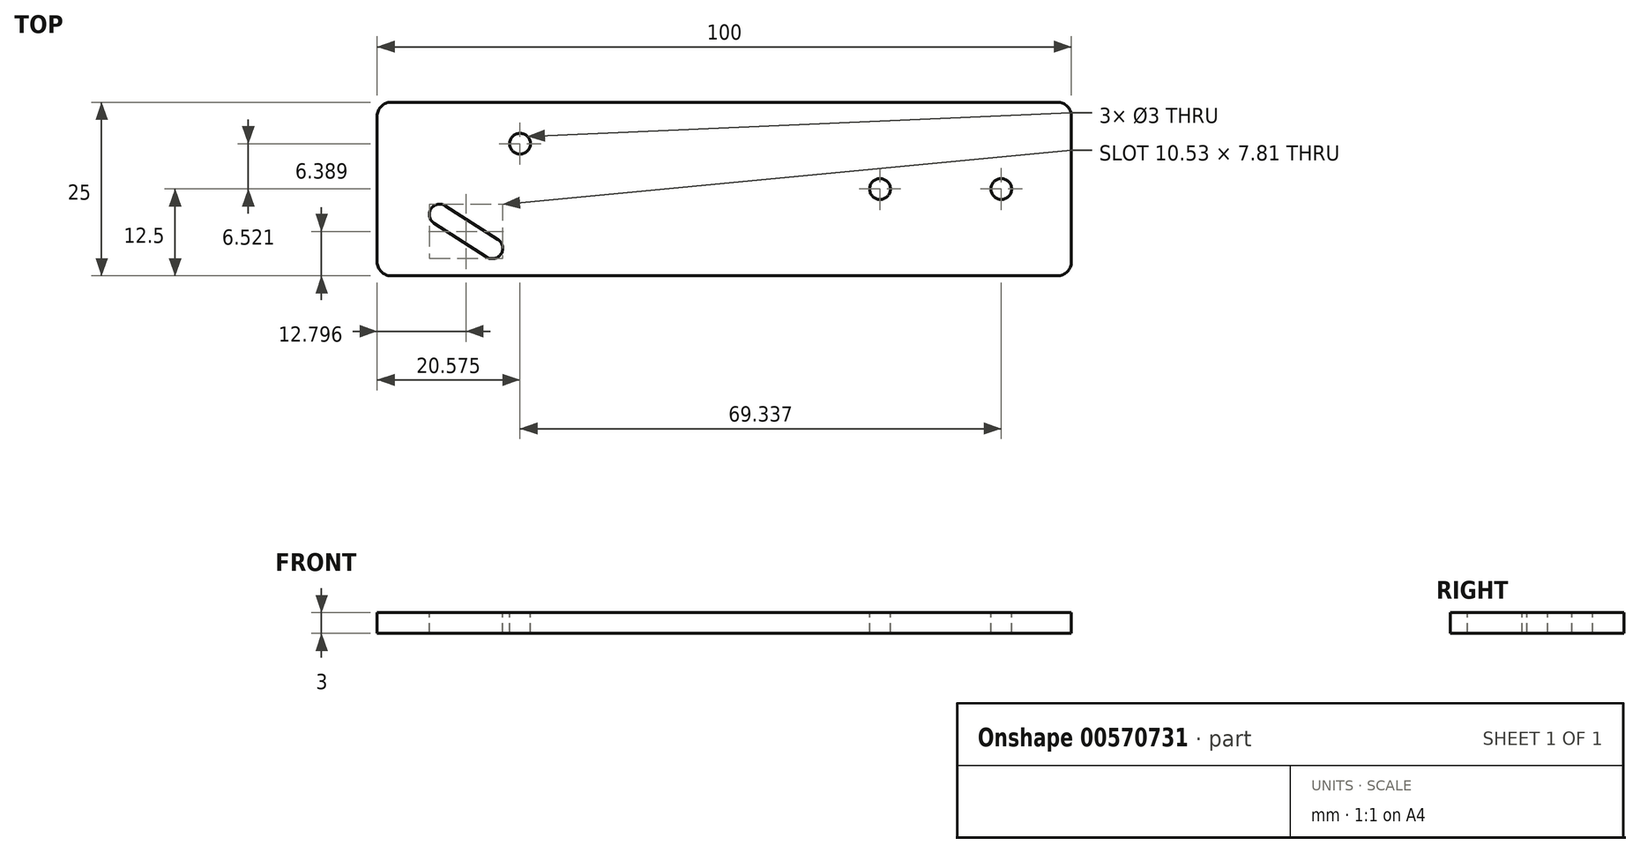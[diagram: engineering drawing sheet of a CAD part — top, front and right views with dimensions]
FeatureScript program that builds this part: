
annotation { "Feature Type Name" : "Feature", "Feature Type Description" : "" }
export const myFeature = defineFeature(function(context is Context, id is Id, definition is map)
    precondition{}
    {
        {
            var Q0;
            Q0=qCreatedBy(makeId("Top.planeOp"),FACE);
            var sketch = newSketch(context, id + "F0", { "sketchPlane" : qUnion([Q0])});
            skLineSegment(sketch, "E0.bottom", {"start": v(48, 12.5) * mm, "end": v(-48, 12.5) * mm});
            skLineSegment(sketch, "E0.top", {"start": v(48, -12.5) * mm, "end": v(-48, -12.5) * mm});
            skLineSegment(sketch, "E0.left", {"start": v(50, 10.5) * mm, "end": v(50, -10.5) * mm});
            skLineSegment(sketch, "E0.right", {"start": v(-50, 10.5) * mm, "end": v(-50, -10.5) * mm});
            skPoint(sketch, "E0.middle", {"position": v(0, 0) * mm});
            skCircle(sketch, "E1", {"center": v(-29.43, 6.52) * mm, "radius": 1.5 * mm});
            skLineSegment(sketch, "E2", {"start": v(-41.8, -4.95) * mm, "end": v(-34.22, -9.8) * mm});
            skLineSegment(sketch, "E3", {"start": v(-32.15, -9.35) * mm, "end": v(-32.15, -9.35) * mm});
            skLineSegment(sketch, "E4", {"start": v(-32.6, -7.28) * mm, "end": v(-40.18, -2.42) * mm});
            skLineSegment(sketch, "E5", {"start": v(-42.26, -2.87) * mm, "end": v(-42.26, -2.87) * mm});
            skPoint(sketch, "E6.visualSharp", {"position": v(-41.45, -1.61) * mm});
            skArc(sketch, "E6.filletArc", {"start": v(-40.18, -2.42) * mm, "mid": v(-41.31, -2.22) * mm, "end": v(-42.26, -2.87) * mm});
            skPoint(sketch, "E7.visualSharp", {"position": v(-43.06, -4.14) * mm});
            skArc(sketch, "E7.filletArc", {"start": v(-42.26, -2.87) * mm, "mid": v(-42.46, -4) * mm, "end": v(-41.8, -4.95) * mm});
            skPoint(sketch, "E8.visualSharp", {"position": v(-32.96, -10.61) * mm});
            skArc(sketch, "E8.filletArc", {"start": v(-34.22, -9.8) * mm, "mid": v(-33.1, -10) * mm, "end": v(-32.15, -9.35) * mm});
            skPoint(sketch, "E9.visualSharp", {"position": v(-31.34, -8.09) * mm});
            skArc(sketch, "E9.filletArc", {"start": v(-32.15, -9.35) * mm, "mid": v(-31.95, -8.22) * mm, "end": v(-32.6, -7.28) * mm});
            skPoint(sketch, "E10.visualSharp", {"position": v(-50, 12.5) * mm});
            skArc(sketch, "E10.filletArc", {"start": v(-48, 12.5) * mm, "mid": v(-49.41, 11.91) * mm, "end": v(-50, 10.5) * mm});
            skPoint(sketch, "E11.visualSharp", {"position": v(-50, -12.5) * mm});
            skArc(sketch, "E11.filletArc", {"start": v(-50, -10.5) * mm, "mid": v(-49.41, -11.91) * mm, "end": v(-48, -12.5) * mm});
            skPoint(sketch, "E12.visualSharp", {"position": v(50, 12.5) * mm});
            skArc(sketch, "E12.filletArc", {"start": v(50, 10.5) * mm, "mid": v(49.41, 11.91) * mm, "end": v(48, 12.5) * mm});
            skPoint(sketch, "E13.visualSharp", {"position": v(50, -12.5) * mm});
            skArc(sketch, "E13.filletArc", {"start": v(48, -12.5) * mm, "mid": v(49.41, -11.91) * mm, "end": v(50, -10.5) * mm});
            skCircle(sketch, "E14", {"center": v(39.91, 0) * mm, "radius": 1.5 * mm});
            skCircle(sketch, "E15", {"center": v(22.44, 0) * mm, "radius": 1.5 * mm});
            skSolve(sketch);
        }
        {
            var Q0;
            Q0 = qSketchRegion(id + "F0", true);
            extrude(context, id + "F1", {"entities" : qUnion([Q0]), "oppositeDirection" : true, "depth" : 3 * mm, "offsetDistance" : 25 * mm});
        }
    });
